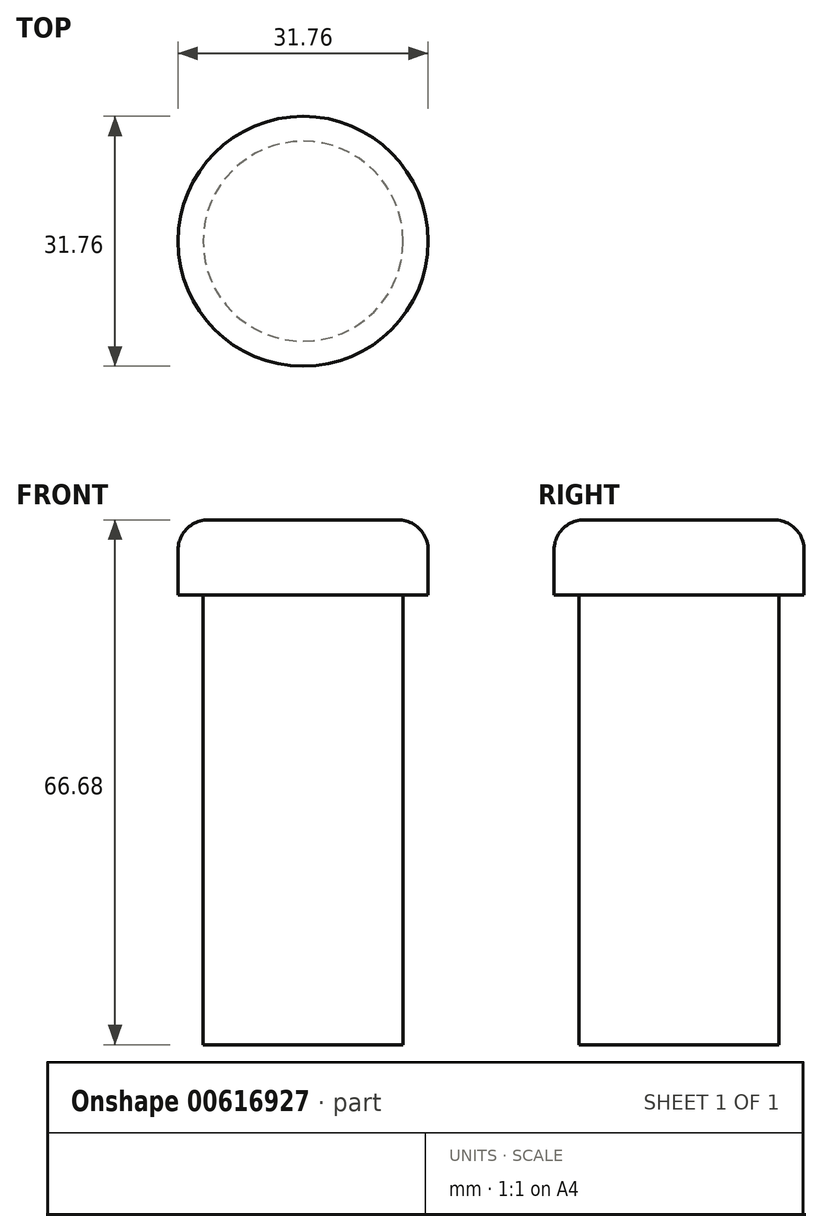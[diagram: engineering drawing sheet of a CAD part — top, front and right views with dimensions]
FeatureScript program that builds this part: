
annotation { "Feature Type Name" : "Feature", "Feature Type Description" : "" }
export const myFeature = defineFeature(function(context is Context, id is Id, definition is map)
    precondition{}
    {
        {
            var Q0;
            Q0=qCreatedBy(makeId("Front.planeOp"),FACE);
            var sketch = newSketch(context, id + "F0", { "sketchPlane" : qUnion([Q0])});
            skLineSegment(sketch, "E0", {"start": v(0, 66.68) * mm, "end": v(0, 0) * mm});
            skLineSegment(sketch, "E1", {"start": v(0, 0) * mm, "end": v(12.7, 0) * mm});
            skLineSegment(sketch, "E2", {"start": v(12.7, 0) * mm, "end": v(12.7, 57.15) * mm});
            skLineSegment(sketch, "E3", {"start": v(12.7, 57.15) * mm, "end": v(15.88, 57.15) * mm});
            skLineSegment(sketch, "E4", {"start": v(15.88, 57.15) * mm, "end": v(15.88, 62.87) * mm});
            skLineSegment(sketch, "E5", {"start": v(15.88, 62.87) * mm, "end": v(12.06, 66.68) * mm, "construction": true});
            skLineSegment(sketch, "E6", {"start": v(12.06, 66.68) * mm, "end": v(0, 66.68) * mm});
            skArc(sketch, "E7", {"start": v(15.88, 62.87) * mm, "mid": v(14.76, 65.56) * mm, "end": v(12.06, 66.68) * mm});
            skSolve(sketch);
        }
        {
            var Q0;
            Q0=makeQuery(id+"F0.imprint","IMPRINT",FACE,{"disambiguationData":[TD([[makeQuery(id+"F0.imprint","IMPRINT",EDGE,{"derivedFrom":sQuery(id+"F0.wireOp",EDGE,"E0")}),1.0]])]});
            var Q1;
            Q1=sQuery(id+"F0.wireOp",EDGE,"E0");
            revolve(context, id + "F1", {"entities" : qUnion([Q0]), "axis" : qUnion([Q1]), "revolveType" : RevolveType.FULL});
        }
    });
